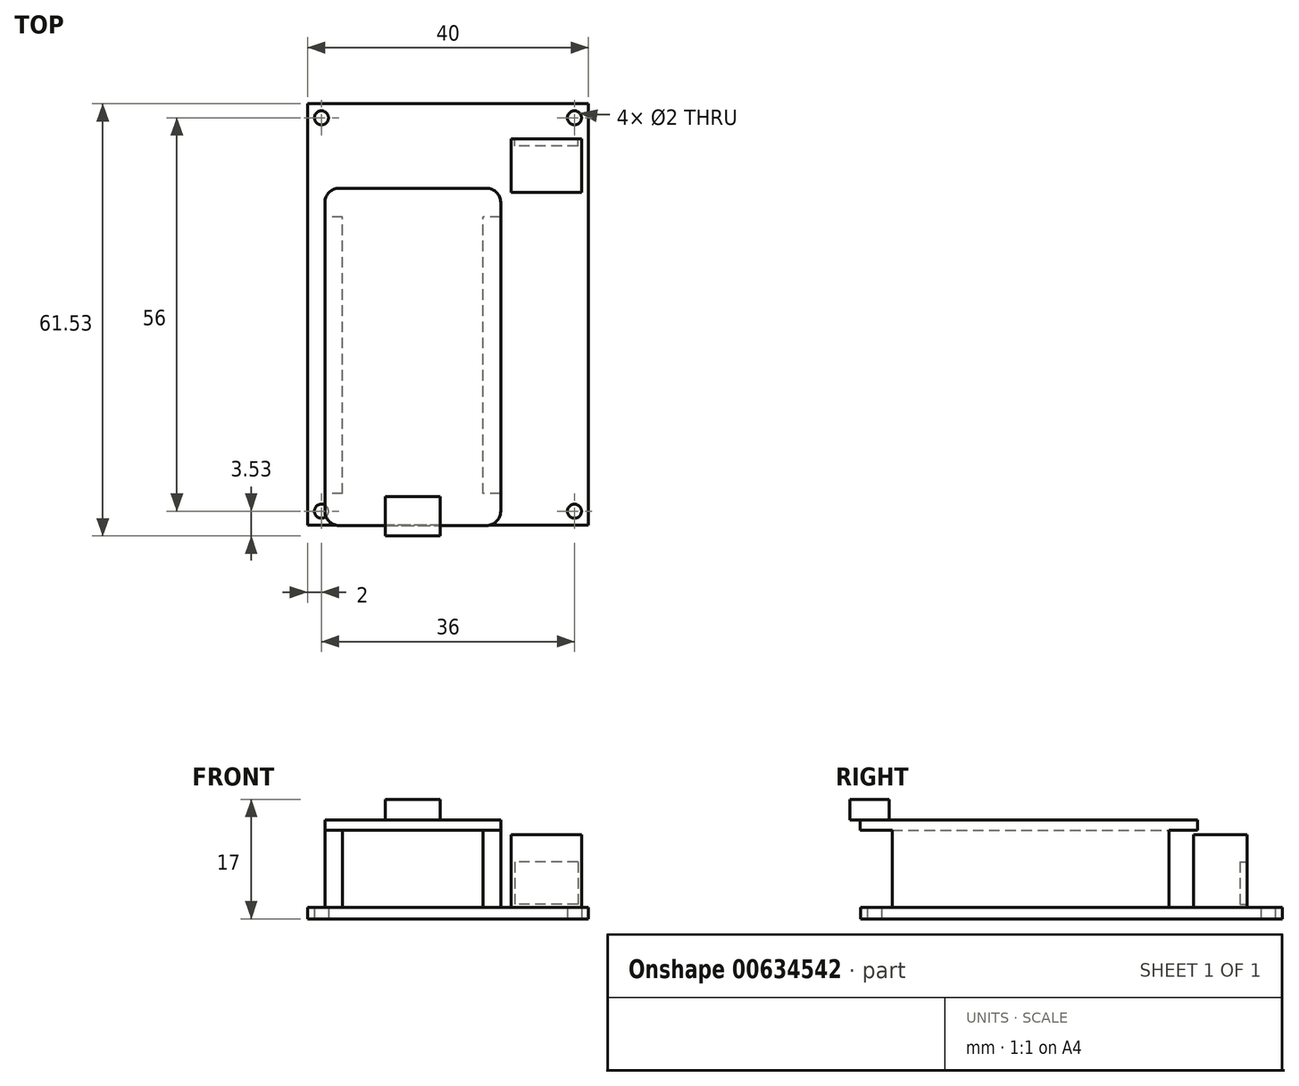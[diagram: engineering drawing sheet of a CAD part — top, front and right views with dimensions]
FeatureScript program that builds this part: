
annotation { "Feature Type Name" : "Feature", "Feature Type Description" : "" }
export const myFeature = defineFeature(function(context is Context, id is Id, definition is map)
    precondition{}
    {
        {
            var Q0;
            Q0=qCreatedBy(makeId("Top.planeOp"),FACE);
            var sketch = newSketch(context, id + "F0", { "sketchPlane" : qUnion([Q0])});
            skLineSegment(sketch, "E0.bottom", {"start": v(20, -30) * mm, "end": v(-20, -30) * mm});
            skLineSegment(sketch, "E0.top", {"start": v(20, 30) * mm, "end": v(-20, 30) * mm});
            skLineSegment(sketch, "E0.left", {"start": v(20, -30) * mm, "end": v(20, 30) * mm});
            skLineSegment(sketch, "E0.right", {"start": v(-20, -30) * mm, "end": v(-20, 30) * mm});
            skPoint(sketch, "E0.middle", {"position": v(0, 0) * mm});
            skCircle(sketch, "E1", {"center": v(-18, 28) * mm, "radius": 1 * mm});
            skCircle(sketch, "E2.0.1.0", {"center": v(-18, -28) * mm, "radius": 1 * mm});
            skCircle(sketch, "E2.1.0.0", {"center": v(18, 28) * mm, "radius": 1 * mm});
            skCircle(sketch, "E2.1.1.0", {"center": v(18, -28) * mm, "radius": 1 * mm});
            skLineSegment(sketch, "E2.direction1", {"start": v(-18, 28) * mm, "end": v(18, 28) * mm, "construction": true});
            skLineSegment(sketch, "E2.direction2", {"start": v(-18, 28) * mm, "end": v(-18, -28) * mm, "construction": true});
            skSolve(sketch);
        }
        {
            var Q0;
            Q0=makeQuery(id+"F0.imprint","IMPRINT",FACE,{"disambiguationData":[TD([[makeQuery(id+"F0.imprint","IMPRINT",EDGE,{"derivedFrom":sQuery(id+"F0.wireOp",EDGE,"E0.bottom")}),-1.0]])]});
            extrude(context, id + "F1", {"entities" : qUnion([Q0]), "depth" : 1.6 * mm, "offsetDistance" : 25 * mm});
        }
        {
            var Q0;
            Q0=makeQuery(id+"F1.opExtrude","CAP_FACE",FACE,{"disambiguationData":[OSD([sQuery(id+"F0.wireOp",EDGE,"E0.bottom"),sQuery(id+"F0.wireOp",EDGE,"E0.top"),sQuery(id+"F0.wireOp",EDGE,"E0.left"),sQuery(id+"F0.wireOp",EDGE,"E0.right"),sQuery(id+"F0.wireOp",EDGE,"E1"),sQuery(id+"F0.wireOp",EDGE,"E2.0.1.0"),sQuery(id+"F0.wireOp",EDGE,"E2.1.0.0"),sQuery(id+"F0.wireOp",EDGE,"E2.1.1.0")])],"isStart":false});
            var sketch = newSketch(context, id + "F2", { "sketchPlane" : qUnion([Q0])});
            skLineSegment(sketch, "E3.bottom", {"start": v(9, 25) * mm, "end": v(19, 25) * mm});
            skLineSegment(sketch, "E3.top", {"start": v(9, 17.4) * mm, "end": v(19, 17.4) * mm});
            skLineSegment(sketch, "E3.left", {"start": v(9, 25) * mm, "end": v(9, 17.4) * mm});
            skLineSegment(sketch, "E3.right", {"start": v(19, 25) * mm, "end": v(19, 17.4) * mm});
            skSolve(sketch);
        }
        {
            var Q0;
            Q0=makeQuery(id+"F2.imprint","IMPRINT",FACE,{"disambiguationData":[TD([[makeQuery(id+"F2.imprint","IMPRINT",EDGE,{"derivedFrom":sQuery(id+"F2.wireOp",EDGE,"E3.bottom")}),-1.0]])]});
            extrude(context, id + "F3", {"entities" : qUnion([Q0]), "operationType" : NewBodyOperationType.ADD, "depth" : 10.4 * mm, "offsetDistance" : 25 * mm});
        }
        {
            var Q0;
            Q0=makeQuery(id+"F3.opExtrude","SWEPT_FACE",FACE,{"disambiguationData":[OSD([sQuery(id+"F2.wireOp",EDGE,"E3.bottom")])]});
            var sketch = newSketch(context, id + "F4", { "sketchPlane" : qUnion([Q0])});
            skLineSegment(sketch, "E4.bottom", {"start": v(-18.5, 8.1) * mm, "end": v(-9.5, 8.1) * mm});
            skLineSegment(sketch, "E4.top", {"start": v(-18.5, 2.1) * mm, "end": v(-9.5, 2.1) * mm});
            skLineSegment(sketch, "E4.left", {"start": v(-18.5, 8.1) * mm, "end": v(-18.5, 2.1) * mm});
            skLineSegment(sketch, "E4.right", {"start": v(-9.5, 8.1) * mm, "end": v(-9.5, 2.1) * mm});
            skSolve(sketch);
        }
        {
            var Q0;
            Q0=makeQuery(id+"F4.imprint","IMPRINT",FACE,{"disambiguationData":[TD([[makeQuery(id+"F4.imprint","IMPRINT",EDGE,{"derivedFrom":sQuery(id+"F4.wireOp",EDGE,"E4.bottom")}),-1.0]])]});
            extrude(context, id + "F5", {"entities" : qUnion([Q0]), "operationType" : NewBodyOperationType.REMOVE, "oppositeDirection" : true, "depth" : 1 * mm, "offsetDistance" : 25 * mm});
        }
        {
            var Q0;
            Q0=makeQuery(id+"F1.opExtrude","CAP_FACE",FACE,{"disambiguationData":[OSD([sQuery(id+"F0.wireOp",EDGE,"E0.bottom"),sQuery(id+"F0.wireOp",EDGE,"E0.top"),sQuery(id+"F0.wireOp",EDGE,"E0.left"),sQuery(id+"F0.wireOp",EDGE,"E0.right"),sQuery(id+"F0.wireOp",EDGE,"E1"),sQuery(id+"F0.wireOp",EDGE,"E2.0.1.0"),sQuery(id+"F0.wireOp",EDGE,"E2.1.0.0"),sQuery(id+"F0.wireOp",EDGE,"E2.1.1.0")])],"isStart":false});
            var sketch = newSketch(context, id + "F6", { "sketchPlane" : qUnion([Q0])});
            skLineSegment(sketch, "E5.bottom", {"start": v(-15, -25.5) * mm, "end": v(-17.5, -25.5) * mm});
            skLineSegment(sketch, "E5.top", {"start": v(-15, 13.9) * mm, "end": v(-17.5, 13.9) * mm});
            skLineSegment(sketch, "E5.left", {"start": v(-15, -25.5) * mm, "end": v(-15, 13.9) * mm});
            skLineSegment(sketch, "E5.right", {"start": v(-17.5, -25.5) * mm, "end": v(-17.5, 13.9) * mm});
            skLineSegment(sketch, "E6.1.0.0", {"start": v(7.5, -25.5) * mm, "end": v(5, -25.5) * mm});
            skLineSegment(sketch, "E6.1.0.1", {"start": v(5, -25.5) * mm, "end": v(5, 13.9) * mm});
            skLineSegment(sketch, "E6.1.0.2", {"start": v(7.5, -25.5) * mm, "end": v(7.5, 13.9) * mm});
            skLineSegment(sketch, "E6.1.0.3", {"start": v(7.5, 13.9) * mm, "end": v(5, 13.9) * mm});
            skLineSegment(sketch, "E6.direction1", {"start": v(-17.5, -25.5) * mm, "end": v(5, -25.5) * mm, "construction": true});
            skSolve(sketch);
        }
        {
            var Q0;
            Q0=makeQuery(id+"F6.imprint","IMPRINT",FACE,{"disambiguationData":[TD([[makeQuery(id+"F6.imprint","IMPRINT",EDGE,{"derivedFrom":sQuery(id+"F6.wireOp",EDGE,"E6.1.0.0")}),-1.0]])]});
            var Q1;
            Q1 = qSketchRegion(id + "F6", true);
            extrude(context, id + "F7", {"entities" : qUnion([Q0, Q1]), "operationType" : NewBodyOperationType.ADD, "depth" : 11 * mm, "offsetDistance" : 25 * mm});
        }
        {
            var Q0;
            Q0=makeQuery(id+"F7.opExtrude","CAP_FACE",FACE,{"disambiguationData":[OSD([sQuery(id+"F6.wireOp",EDGE,"E5.bottom"),sQuery(id+"F6.wireOp",EDGE,"E5.top"),sQuery(id+"F6.wireOp",EDGE,"E5.left"),sQuery(id+"F6.wireOp",EDGE,"E5.right")])],"isStart":false});
            var sketch = newSketch(context, id + "F8", { "sketchPlane" : qUnion([Q0])});
            skLineSegment(sketch, "E7.bottom", {"start": v(-17.5, -30.03) * mm, "end": v(7.5, -30.03) * mm});
            skLineSegment(sketch, "E7.top", {"start": v(-17.5, 17.97) * mm, "end": v(7.5, 17.97) * mm});
            skLineSegment(sketch, "E7.left", {"start": v(-17.5, -30.03) * mm, "end": v(-17.5, 17.97) * mm});
            skLineSegment(sketch, "E7.right", {"start": v(7.5, -30.03) * mm, "end": v(7.5, 17.97) * mm});
            skSolve(sketch);
        }
        {
            var Q0;
            Q0 = qSketchRegion(id + "F8", true);
            extrude(context, id + "F9", {"entities" : qUnion([Q0]), "operationType" : NewBodyOperationType.ADD, "depth" : 1.5 * mm, "offsetDistance" : 25 * mm});
        }
        {
            var Q0;
            Q0=makeQuery(id+"F9.opExtrude","SWEPT_EDGE",EDGE,{"disambiguationData":[OSD([sQuery(id+"F8.wireOp",EDGE,"E7.bottom"),sQuery(id+"F8.wireOp",EDGE,"E7.left")])]});
            var Q1;
            Q1=makeQuery(id+"F9.opExtrude","SWEPT_EDGE",EDGE,{"disambiguationData":[OSD([sQuery(id+"F8.wireOp",EDGE,"E7.bottom"),sQuery(id+"F8.wireOp",EDGE,"E7.right")])]});
            var Q2;
            Q2=makeQuery(id+"F9.opExtrude","SWEPT_EDGE",EDGE,{"disambiguationData":[OSD([sQuery(id+"F8.wireOp",EDGE,"E7.top"),sQuery(id+"F8.wireOp",EDGE,"E7.right")])]});
            var Q3;
            Q3=makeQuery(id+"F9.opExtrude","SWEPT_EDGE",EDGE,{"disambiguationData":[OSD([sQuery(id+"F8.wireOp",EDGE,"E7.top"),sQuery(id+"F8.wireOp",EDGE,"E7.left")])]});
            fillet(context, id + "F10", {"entities" : qUnion([Q0, Q1, Q2, Q3]), "radius" : 2 * mm, "tangentPropagation" : true, "allowEdgeOverflow" : false});
        }
        {
            var Q0;
            Q0=makeQuery(id+"F9.opExtrude","CAP_FACE",FACE,{"disambiguationData":[OSD([sQuery(id+"F8.wireOp",EDGE,"E7.bottom"),sQuery(id+"F8.wireOp",EDGE,"E7.top"),sQuery(id+"F8.wireOp",EDGE,"E7.left"),sQuery(id+"F8.wireOp",EDGE,"E7.right")])],"isStart":false});
            var sketch = newSketch(context, id + "F11", { "sketchPlane" : qUnion([Q0])});
            skLineSegment(sketch, "E8.bottom", {"start": v(-8.9, -25.93) * mm, "end": v(-1.1, -25.93) * mm});
            skLineSegment(sketch, "E8.top", {"start": v(-8.9, -31.53) * mm, "end": v(-1.1, -31.53) * mm});
            skLineSegment(sketch, "E8.left", {"start": v(-8.9, -25.93) * mm, "end": v(-8.9, -31.53) * mm});
            skLineSegment(sketch, "E8.right", {"start": v(-1.1, -25.93) * mm, "end": v(-1.1, -31.53) * mm});
            skSolve(sketch);
        }
        {
            var Q0;
            Q0 = qSketchRegion(id + "F11", true);
            extrude(context, id + "F12", {"entities" : qUnion([Q0]), "operationType" : NewBodyOperationType.ADD, "depth" : 2.9 * mm, "offsetDistance" : 25 * mm});
        }
    });
